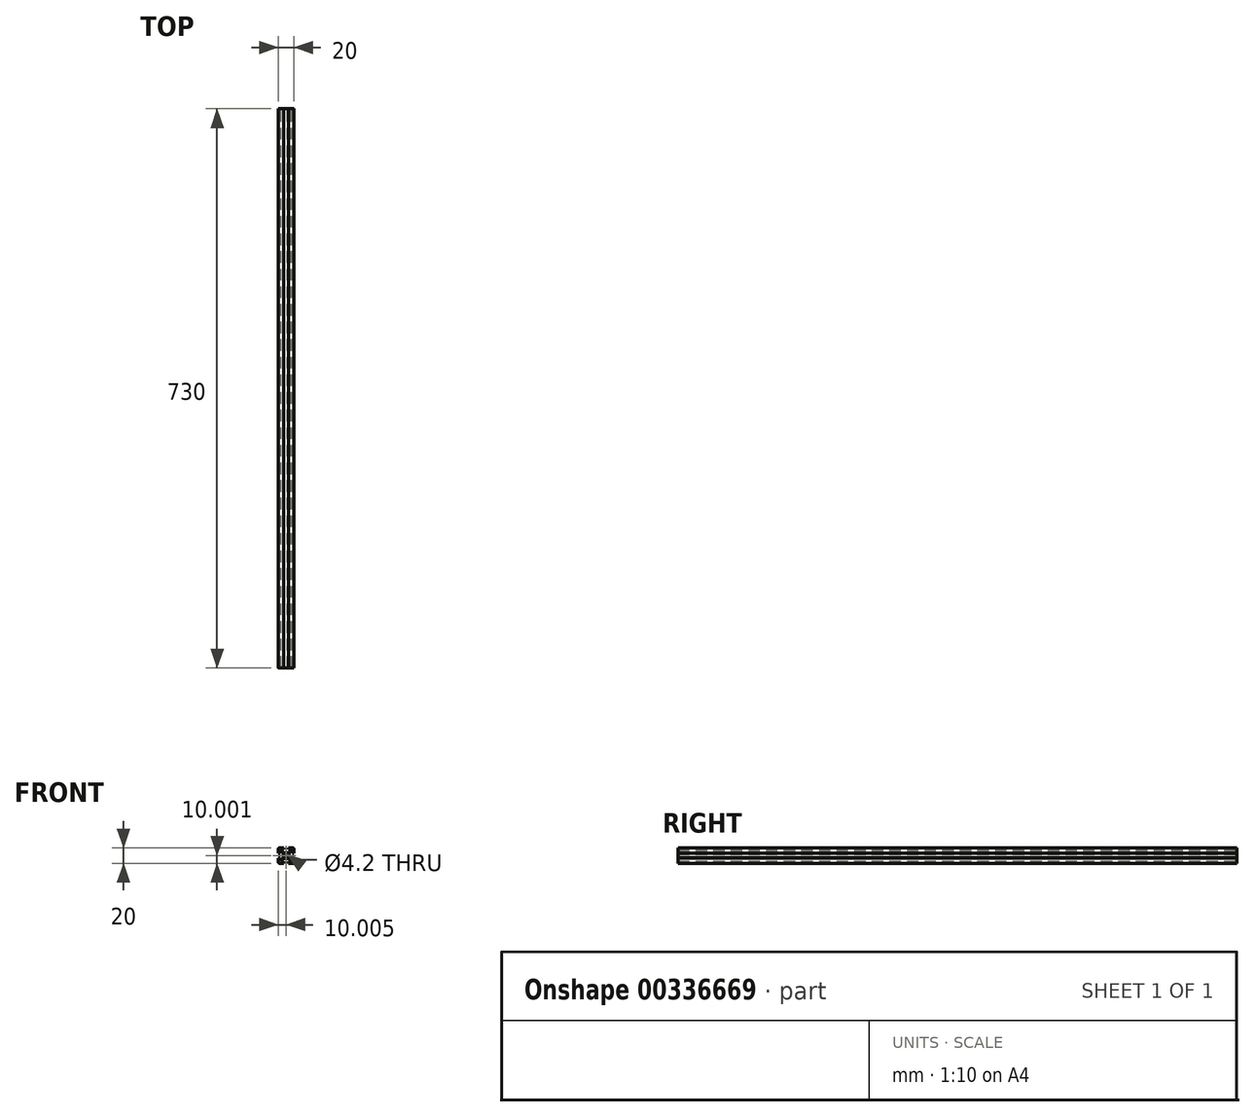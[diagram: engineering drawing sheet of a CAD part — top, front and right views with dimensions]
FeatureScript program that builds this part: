
annotation { "Feature Type Name" : "Feature", "Feature Type Description" : "" }
export const myFeature = defineFeature(function(context is Context, id is Id, definition is map)
    precondition{}
    {
        {
            var Q0;
            Q0=qCreatedBy(makeId("Front.planeOp"),FACE);
            var sketch = newSketch(context, id + "F0", { "sketchPlane" : qUnion([Q0])});
            skCircle(sketch, "E0", {"center": v(-0.06, -0.16) * mm, "radius": 2.1 * mm});
            skLineSegment(sketch, "E1.bottom", {"start": v(8.94, 9.84) * mm, "end": v(2.94, 9.84) * mm});
            skLineSegment(sketch, "E1.top", {"start": v(8.94, -10.16) * mm, "end": v(2.94, -10.16) * mm});
            skLineSegment(sketch, "E1.left", {"start": v(9.94, 8.84) * mm, "end": v(9.94, 2.84) * mm});
            skLineSegment(sketch, "E1.right", {"start": v(-10.06, 8.84) * mm, "end": v(-10.06, 2.84) * mm});
            skLineSegment(sketch, "E2.bottom", {"start": v(2.88, 3.84) * mm, "end": v(-3, 3.84) * mm});
            skLineSegment(sketch, "E2.top", {"start": v(2.88, -4.16) * mm, "end": v(-3, -4.16) * mm});
            skLineSegment(sketch, "E2.left", {"start": v(3.94, 2.78) * mm, "end": v(3.94, -3.1) * mm});
            skLineSegment(sketch, "E2.right", {"start": v(-4.06, 2.78) * mm, "end": v(-4.06, -3.1) * mm});
            skLineSegment(sketch, "E3.bottom", {"start": v(6.88, 7.84) * mm, "end": v(2.94, 7.84) * mm});
            skLineSegment(sketch, "E3.top", {"start": v(6.88, -8.16) * mm, "end": v(2.94, -8.16) * mm});
            skLineSegment(sketch, "E3.left", {"start": v(7.94, 6.78) * mm, "end": v(7.94, 2.84) * mm});
            skLineSegment(sketch, "E3.right", {"start": v(-8.06, 6.78) * mm, "end": v(-8.06, 2.84) * mm});
            skLineSegment(sketch, "E4", {"start": v(-3.06, -10.16) * mm, "end": v(-3.06, -8.16) * mm});
            skLineSegment(sketch, "E5.MirrorCS", {"start": v(2.94, -10.16) * mm, "end": v(2.94, -8.16) * mm});
            skLineSegment(sketch, "E6.MirrorCS", {"start": v(-3.06, 9.84) * mm, "end": v(-3.06, 7.84) * mm});
            skLineSegment(sketch, "E7.MirrorCS", {"start": v(2.94, 9.84) * mm, "end": v(2.94, 7.84) * mm});
            skLineSegment(sketch, "E8", {"start": v(-10.06, 2.84) * mm, "end": v(-8.06, 2.84) * mm});
            skLineSegment(sketch, "E9.MirrorCS", {"start": v(-10.06, -3.16) * mm, "end": v(-8.06, -3.16) * mm});
            skLineSegment(sketch, "E10", {"start": v(7.94, 2.84) * mm, "end": v(9.94, 2.84) * mm});
            skLineSegment(sketch, "E11.MirrorCS", {"start": v(7.94, -3.16) * mm, "end": v(9.94, -3.16) * mm});
            skPoint(sketch, "E12", {"position": v(-8.06, -7.1) * mm});
            skPoint(sketch, "E13", {"position": v(6.88, 7.84) * mm});
            skPoint(sketch, "E14", {"position": v(-4.06, -3.1) * mm});
            skPoint(sketch, "E15", {"position": v(2.88, 3.84) * mm});
            skLineSegment(sketch, "E16", {"start": v(-8.06, -7.1) * mm, "end": v(-4.06, -3.1) * mm});
            skLineSegment(sketch, "E17", {"start": v(2.88, 3.84) * mm, "end": v(6.88, 7.84) * mm});
            skLineSegment(sketch, "E18.MirrorCS", {"start": v(-7, -8.16) * mm, "end": v(-3, -4.16) * mm});
            skLineSegment(sketch, "E19.1.0", {"start": v(6.88, -8.16) * mm, "end": v(2.88, -4.16) * mm});
            skLineSegment(sketch, "E19.2.0", {"start": v(7.94, 6.78) * mm, "end": v(3.94, 2.78) * mm});
            skLineSegment(sketch, "E19.3.0", {"start": v(-7, 7.84) * mm, "end": v(-3, 3.84) * mm});
            skLineSegment(sketch, "E20.1.0", {"start": v(7.94, -7.1) * mm, "end": v(3.94, -3.1) * mm});
            skLineSegment(sketch, "E20.2.0", {"start": v(6.88, 7.84) * mm, "end": v(2.88, 3.84) * mm});
            skLineSegment(sketch, "E20.3.0", {"start": v(-8.06, 6.78) * mm, "end": v(-4.06, 2.78) * mm});
            skLineSegment(sketch, "E21.trimOffspring", {"start": v(-3.06, 7.84) * mm, "end": v(-7, 7.84) * mm});
            skLineSegment(sketch, "E22.trimOffspring", {"start": v(-3.06, 9.84) * mm, "end": v(-9.06, 9.84) * mm});
            skLineSegment(sketch, "E23.trimOffspring", {"start": v(7.94, -3.16) * mm, "end": v(7.94, -7.1) * mm});
            skLineSegment(sketch, "E24.trimOffspring", {"start": v(9.94, -3.16) * mm, "end": v(9.94, -9.16) * mm});
            skLineSegment(sketch, "E25.trimOffspring", {"start": v(-3.06, -10.16) * mm, "end": v(-9.06, -10.16) * mm});
            skLineSegment(sketch, "E26.trimOffspring", {"start": v(-3.06, -8.16) * mm, "end": v(-7, -8.16) * mm});
            skLineSegment(sketch, "E27.trimOffspring", {"start": v(-10.06, -3.16) * mm, "end": v(-10.06, -9.16) * mm});
            skLineSegment(sketch, "E28.trimOffspring", {"start": v(-8.06, -3.16) * mm, "end": v(-8.06, -7.1) * mm});
            skArc(sketch, "E29.filletArc", {"start": v(-10.06, -9.16) * mm, "mid": v(-9.76, -9.87) * mm, "end": v(-9.06, -10.16) * mm});
            skArc(sketch, "E30.filletArc", {"start": v(8.94, -10.16) * mm, "mid": v(9.65, -9.87) * mm, "end": v(9.94, -9.16) * mm});
            skArc(sketch, "E31.filletArc", {"start": v(9.94, 8.84) * mm, "mid": v(9.65, 9.55) * mm, "end": v(8.94, 9.84) * mm});
            skArc(sketch, "E32.filletArc", {"start": v(-9.06, 9.84) * mm, "mid": v(-9.76, 9.55) * mm, "end": v(-10.06, 8.84) * mm});
            skSolve(sketch);
        }
        {
            var Q0;
            Q0=makeQuery(id+"F0.imprint","IMPRINT",FACE,{"disambiguationData":[TD([[makeQuery(id+"F0.imprint","IMPRINT",EDGE,{"derivedFrom":sQuery(id+"F0.wireOp",EDGE,"E0")}),-1.0]])]});
            extrude(context, id + "F1", {"entities" : qUnion([Q0]), "depth" : 730 * mm});
        }
    });
